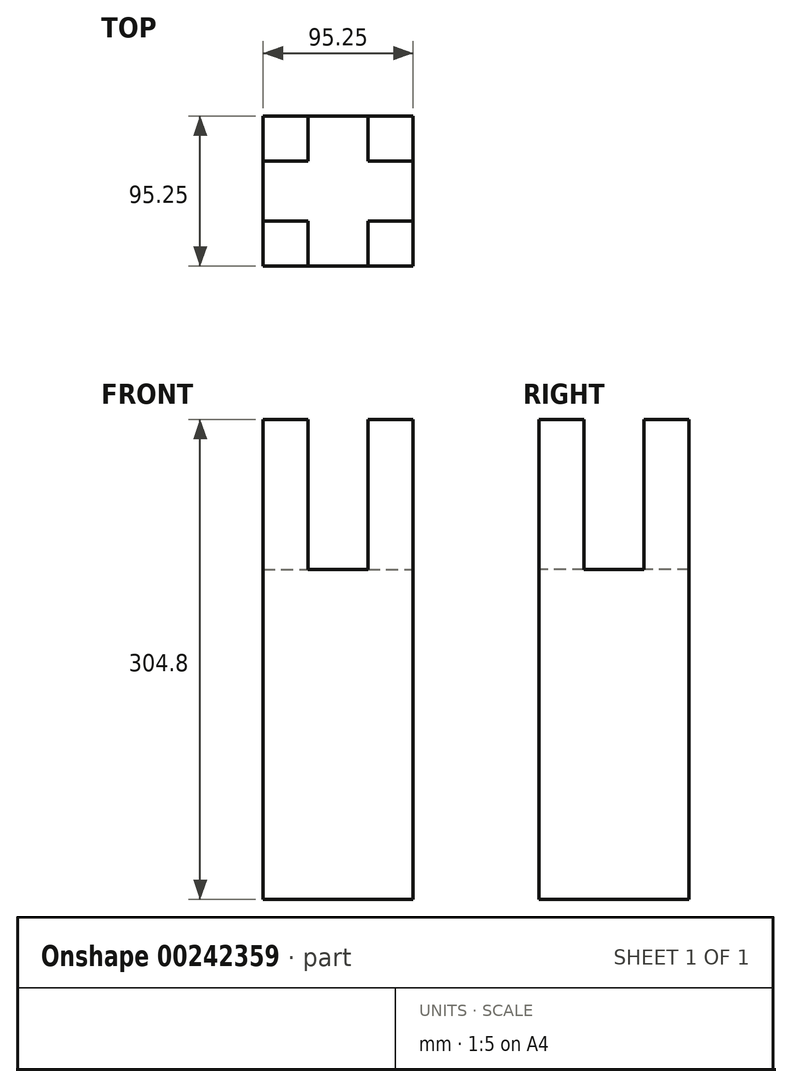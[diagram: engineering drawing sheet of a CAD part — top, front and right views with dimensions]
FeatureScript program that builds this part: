
annotation { "Feature Type Name" : "Feature", "Feature Type Description" : "" }
export const myFeature = defineFeature(function(context is Context, id is Id, definition is map)
    precondition{}
    {
        {
            var Q0;
            Q0=qCreatedBy(makeId("Top.planeOp"),FACE);
            var sketch = newSketch(context, id + "F0", { "sketchPlane" : qUnion([Q0])});
            skLineSegment(sketch, "E0.bottom", {"start": v(0, 0) * mm, "end": v(95.25, 0) * mm});
            skLineSegment(sketch, "E0.top", {"start": v(0, 95.25) * mm, "end": v(95.25, 95.25) * mm});
            skLineSegment(sketch, "E0.left", {"start": v(0, 0) * mm, "end": v(0, 95.25) * mm});
            skLineSegment(sketch, "E0.right", {"start": v(95.25, 0) * mm, "end": v(95.25, 95.25) * mm});
            skSolve(sketch);
        }
        {
            var Q0;
            Q0=qCreatedBy(makeId("Top.planeOp"),FACE);
            var sketch = newSketch(context, id + "F1", { "sketchPlane" : qUnion([Q0])});
            skLineSegment(sketch, "E1.bottom", {"start": v(28.57, 95.25) * mm, "end": v(66.67, 95.25) * mm});
            skLineSegment(sketch, "E1.top", {"start": v(28.57, 0) * mm, "end": v(66.67, 0) * mm});
            skLineSegment(sketch, "E1.left", {"start": v(28.57, 95.25) * mm, "end": v(28.57, 0) * mm});
            skLineSegment(sketch, "E1.right", {"start": v(66.67, 95.25) * mm, "end": v(66.67, 0) * mm});
            skLineSegment(sketch, "E2.bottom", {"start": v(0, 66.68) * mm, "end": v(95.25, 66.68) * mm});
            skLineSegment(sketch, "E2.top", {"start": v(0, 28.57) * mm, "end": v(95.25, 28.57) * mm});
            skLineSegment(sketch, "E2.left", {"start": v(0, 66.68) * mm, "end": v(0, 28.57) * mm});
            skLineSegment(sketch, "E2.right", {"start": v(95.25, 66.68) * mm, "end": v(95.25, 28.58) * mm});
            skPoint(sketch, "E3", {"position": v(47.62, 95.25) * mm});
            skPoint(sketch, "E4", {"position": v(95.25, 47.63) * mm});
            skSolve(sketch);
        }
        {
            var Q0;
            Q0=makeQuery(id+"F0.imprint","IMPRINT",FACE,{"disambiguationData":[TD([[makeQuery(id+"F0.imprint","IMPRINT",EDGE,{"derivedFrom":sQuery(id+"F0.wireOp",EDGE,"E0.bottom")}),1.0]])]});
            extrude(context, id + "F2", {"entities" : qUnion([Q0]), "depth" : 304.8 * mm});
        }
        {
            var Q0;
            {var subQ5=sQuery(id+"F1.wireOp",EDGE,"E2.left");Q0=makeQuery(id+"F1.imprint","IMPRINT",FACE,{"disambiguationData":[TD([[makeQuery(id+"F1.imprint","IMPRINT",EDGE,{"derivedFrom":subQ5}),1.0]])]});}
            var Q1;
            {var subQ0=sQuery(id+"F1.wireOp",EDGE,"E2.bottom");var subQ1=sQuery(id+"F1.wireOp",EDGE,"E1.left");var subQ2=makeQuery(id+"F1.imprint","INTERSECT",VERTEX,{"derivedFrom":[subQ1,subQ0]});Q1=makeQuery(id+"F1.imprint","IMPRINT",FACE,{"disambiguationData":[TD([[makeQuery(id+"F1.imprint","IMPRINT",EDGE,{"disambiguationData":[TD([[subQ2,-1.0]])],"derivedFrom":subQ1}),1.0]])]});}
            var Q2;
            {var subQ5=sQuery(id+"F1.wireOp",EDGE,"E2.right");Q2=makeQuery(id+"F1.imprint","IMPRINT",FACE,{"disambiguationData":[TD([[makeQuery(id+"F1.imprint","IMPRINT",EDGE,{"derivedFrom":subQ5}),-1.0]])]});}
            var Q3;
            {var subQ0=sQuery(id+"F1.wireOp",EDGE,"E1.bottom");Q3=makeQuery(id+"F1.imprint","IMPRINT",FACE,{"disambiguationData":[TD([[makeQuery(id+"F1.imprint","IMPRINT",EDGE,{"derivedFrom":subQ0}),-1.0]])]});}
            var Q4;
            {var subQ0=sQuery(id+"F1.wireOp",EDGE,"E1.top");Q4=makeQuery(id+"F1.imprint","IMPRINT",FACE,{"disambiguationData":[TD([[makeQuery(id+"F1.imprint","IMPRINT",EDGE,{"derivedFrom":subQ0}),1.0]])]});}
            extrude(context, id + "F3", {"entities" : qUnion([Q0, Q1, Q2, Q3, Q4]), "operationType" : NewBodyOperationType.REMOVE, "depth" : 304.8 * mm, "hasSecondDirection" : true, "secondDirectionOppositeDirection" : false, "secondDirectionDepth" : 209.55 * mm});
        }
    });
